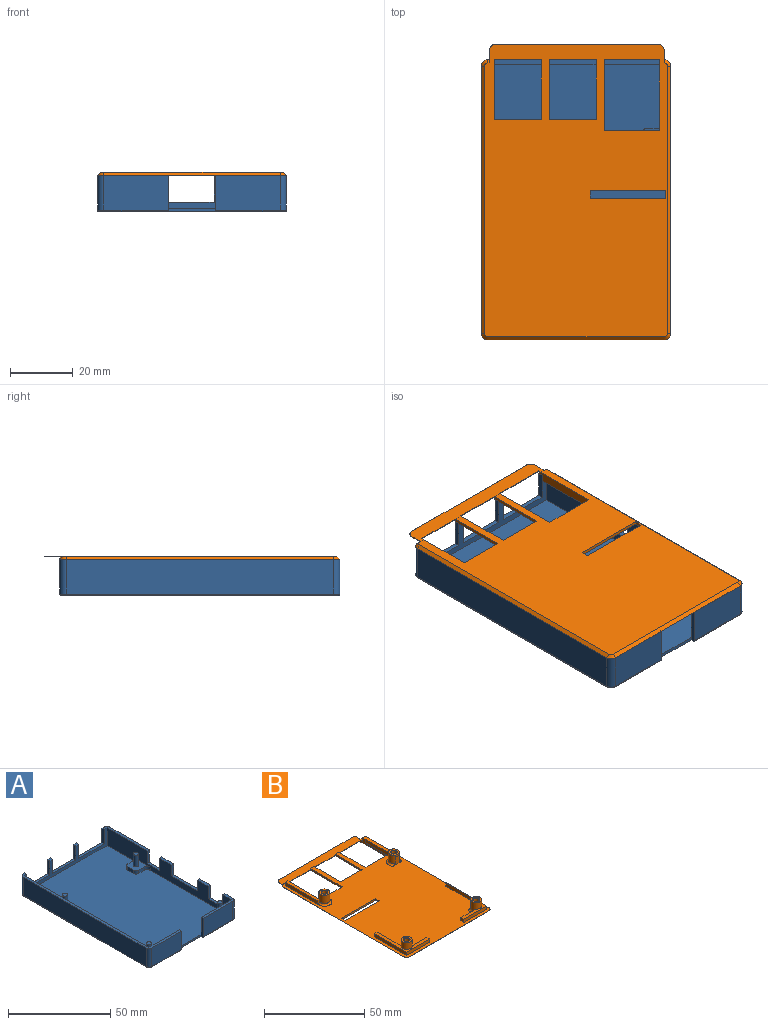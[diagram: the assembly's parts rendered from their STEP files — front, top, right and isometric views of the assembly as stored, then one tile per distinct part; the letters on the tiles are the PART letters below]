
ASSEMBLY  parts=2 mates=1
PART A: 89 faces, bbox 60.3x89.3x11.5 mm
  f0: plane 8.25x1.5mm, normal (0,0,1), area 12.4mm2, adj f3,f17,f84,f88
  f1: plane 29.25x3.5mm, normal (0,0,1), area 46mm2, adj f3,f16,f17,f18,f21,f70,f85
  f2: plane 7.5x1.5mm, normal (0,0,1), area 11.2mm2, adj f3,f17,f82,f87
  f3: plane 86x10.5mm, normal (-1,0,0), area 604.7mm2, adj f0,f1,f2,f4,f5,f8,f18,f35
  f4: plane 21x10.5mm, normal (0,1,0), area 201mm2, adj f3,f5,f8,f30,f39,f54
  f5: plane 86x57mm, normal (0,0,1), area 4663.9mm2, adj f3,f4,f6,f7,f18,f28,f32,f33
  f6: plane 86x10.5mm, normal (1,0,0), area 860.5mm2, adj f5,f7,f12,f18,f31,f42,f58,f59
  f7: plane 21x10.5mm, normal (0,1,0), area 201mm2, adj f5,f6,f12,f29,f42,f53
  f8: plane 22.5x7.5mm, normal (0,0,1), area 41.9mm2, adj f3,f4,f9,f17,f30,f69,f81
  f9: plane 20.5x11mm, normal (0,-1,0), area 225.5mm2, adj f8,f30,f69,f79
  f10: plane 2x1.5mm, normal (0,0,1), area 3mm2, adj f16,f18,f23,f27
  f11: plane 2x1.5mm, normal (0,0,1), area 3mm2, adj f16,f18,f20,f24
  f12: plane 89x22.5mm, normal (0,0,1), area 165.5mm2, adj f6,f7,f13,f15,f16,f18,f26,f29
  f13: plane 85x11mm, normal (-1,0,0), area 935mm2, adj f12,f67,f68,f73
  f14: plane 88x59mm, normal (0,0,-1), area 5175.1mm2, adj f28,f29,f30,f71,f72,f73,f74,f75
  f15: plane 20.5x11mm, normal (0,-1,0), area 225.5mm2, adj f12,f29,f68,f71
  f16: plane 56x11mm, normal (0,1,0), area 195.3mm2, adj f1,f10,f11,f12,f19,f20,f21,f22
  f17: plane 85x11mm, normal (1,0,0), area 679.2mm2, adj f0,f1,f2,f8,f69,f70,f77,f80
  f18: plane 57x10.5mm, normal (0,-1,0), area 177.8mm2, adj f1,f3,f5,f6,f10,f11,f12,f19
  f19: plane 17.5x1.5mm, normal (0,0,1), area 26.2mm2, adj f16,f18,f20,f21
  f20: plane 8.5x1.5mm, normal (1,0,0), area 12.8mm2, adj f11,f16,f18,f19
  f21: plane 8.5x1.5mm, normal (-1,0,0), area 12.8mm2, adj f1,f16,f18,f19
  f22: plane 16x1.5mm, normal (0,0,1), area 24mm2, adj f16,f18,f23,f24
  f23: plane 8.5x1.5mm, normal (1,0,0), area 12.8mm2, adj f10,f16,f18,f22
  f24: plane 8.5x1.5mm, normal (-1,0,0), area 12.8mm2, adj f11,f16,f18,f22
  f25: plane 16x1.5mm, normal (0,0,1), area 24mm2, adj f16,f18,f26,f27
  f26: plane 8.5x1.5mm, normal (1,0,0), area 12.8mm2, adj f12,f16,f18,f25
  f27: plane 8.5x1.5mm, normal (-1,0,0), area 12.8mm2, adj f10,f16,f18,f25
  f28: plane 15x1mm, normal (0,-1,0), area 15mm2, adj f5,f14,f29,f30
  f29: plane 11.5x1.5mm, normal (1,0,0), area 17.2mm2, adj f7,f12,f14,f15,f28,f71
  f30: plane 11.5x1.5mm, normal (-1,0,0), area 17.2mm2, adj f4,f8,f9,f14,f28,f79
  f31: plane 11.5x7.75mm, normal (0,0,1), area 53.2mm2, adj f6,f32,f33,f34,f46,f59,f60,f65
  f32: plane 3.75x2mm, normal (0,-1,0), area 7.5mm2, adj f5,f31,f59,f65
  f33: plane 3.75x2mm, normal (0,1,0), area 7.5mm2, adj f5,f31,f60,f66
  f34: plane 3.5x2mm, normal (1,0,0), area 7mm2, adj f5,f31,f65,f66
  f35: plane 11.5x7.75mm, normal (0,0,1), area 53.2mm2, adj f3,f36,f37,f38,f48,f55,f56,f63
  f36: plane 3.5x2mm, normal (-1,0,0), area 7mm2, adj f5,f35,f63,f64
  f37: plane 3.75x2mm, normal (0,-1,0), area 7.5mm2, adj f5,f35,f55,f64
  f38: plane 3.75x2mm, normal (0,1,0), area 7.5mm2, adj f5,f35,f56,f63
  f39: plane 9.75x9.75mm, normal (0,0,1), area 56mm2, adj f3,f4,f40,f41,f50,f54,f57,f61
  f40: plane 3.75x2mm, normal (-1,0,0), area 7.5mm2, adj f5,f39,f54,f61
  f41: plane 3.75x2mm, normal (0,1,0), area 7.5mm2, adj f5,f39,f57,f61
  f42: plane 9.75x9.75mm, normal (0,0,1), area 56mm2, adj f6,f7,f43,f44,f52,f53,f58,f62
  f43: plane 3.75x2mm, normal (0,1,0), area 7.5mm2, adj f5,f42,f58,f62
  f44: plane 3.75x2mm, normal (1,0,0), area 7.5mm2, adj f5,f42,f53,f62
  f45: plane 2.5x2.5mm, normal (0,0,1), area 4.9mm2, adj f46
  f46: cylinder r=1.25mm len=7mm, axis (0,0,-1), area 55mm2, adj f31,f45
  f47: plane 2.5x2.5mm, normal (0,0,1), area 4.9mm2, adj f48
  f48: cylinder r=1.25mm len=7mm, axis (0,0,-1), area 55mm2, adj f35,f47
  f49: plane 2.5x2.5mm, normal (0,0,1), area 4.9mm2, adj f50
  f50: cylinder r=1.25mm len=7mm, axis (0,0,-1), area 55mm2, adj f39,f49
  f51: plane 2.5x2.5mm, normal (0,0,1), area 4.9mm2, adj f52
  f52: cylinder r=1.25mm len=7mm, axis (0,0,-1), area 55mm2, adj f42,f51
  f53: cylinder r=2mm len=2mm, axis (0,0,-1), area 6.3mm2, adj f5,f7,f42,f44
  f54: cylinder r=2mm len=2mm, axis (0,0,1), area 6.3mm2, adj f4,f5,f39,f40
  f55: cylinder r=2mm len=2mm, axis (0,0,1), area 6.3mm2, adj f3,f5,f35,f37
  f56: cylinder r=2mm len=2mm, axis (0,0,-1), area 6.3mm2, adj f3,f5,f35,f38
  f57: cylinder r=2mm len=2mm, axis (0,0,-1), area 6.3mm2, adj f3,f5,f39,f41
  f58: cylinder r=2mm len=2mm, axis (0,0,-1), area 6.3mm2, adj f5,f6,f42,f43
  f59: cylinder r=2mm len=2mm, axis (0,0,1), area 6.3mm2, adj f5,f6,f31,f32
  f60: cylinder r=2mm len=2mm, axis (0,0,-1), area 6.3mm2, adj f5,f6,f31,f33
  f61: cylinder r=2mm len=2mm, axis (0,0,1), area 6.3mm2, adj f5,f39,f40,f41
  f62: cylinder r=2mm len=2mm, axis (0,0,-1), area 6.3mm2, adj f5,f42,f43,f44
  f63: cylinder r=2mm len=2mm, axis (0,0,1), area 6.3mm2, adj f5,f35,f36,f38
  f64: cylinder r=2mm len=2mm, axis (0,0,-1), area 6.3mm2, adj f5,f35,f36,f37
  f65: cylinder r=2mm len=2mm, axis (0,0,1), area 6.3mm2, adj f5,f31,f32,f34
  f66: cylinder r=2mm len=2mm, axis (0,0,-1), area 6.3mm2, adj f5,f31,f33,f34
  f67: cylinder r=2mm len=11mm, axis (0,0,1), area 34.6mm2, adj f12,f13,f16,f74
  f68: cylinder r=2mm len=11mm, axis (0,0,-1), area 34.6mm2, adj f12,f13,f15,f72
  f69: cylinder r=2mm len=11mm, axis (0,0,1), area 34.6mm2, adj f8,f9,f17,f78
  f70: cylinder r=2mm len=11mm, axis (0,0,-1), area 34.6mm2, adj f1,f16,f17,f76
  f71: cylinder r=0.5mm len=20.5mm, axis (1,0,0), area 16.1mm2, adj f14,f15,f29,f72
  f72: torus R=1.5mm, axis (0,0,1), area 2.2mm2, adj f14,f68,f71,f73
  f73: cylinder r=0.5mm len=85mm, axis (0,-1,0), area 66.8mm2, adj f13,f14,f72,f74
  f74: torus R=1.5mm, axis (0,0,1), area 2.2mm2, adj f14,f67,f73,f75
  f75: cylinder r=0.5mm len=56mm, axis (-1,0,0), area 44mm2, adj f14,f16,f74,f76
  f76: torus R=1.5mm, axis (0,0,1), area 2.2mm2, adj f14,f70,f75,f77
  f77: cylinder r=0.5mm len=85mm, axis (0,1,0), area 66.8mm2, adj f14,f17,f76,f78
  f78: torus R=1.5mm, axis (0,0,1), area 2.2mm2, adj f14,f69,f77,f79
  f79: cylinder r=0.5mm len=20.5mm, axis (1,0,0), area 16.1mm2, adj f9,f14,f30,f78
  f80: plane 10x1.5mm, normal (0,0,1), area 15mm2, adj f3,f17,f81,f82
  f81: plane 7.5x1.5mm, normal (0,1,0), area 11.2mm2, adj f3,f8,f17,f80
  f82: plane 7.5x1.5mm, normal (0,-1,0), area 11.2mm2, adj f2,f3,f17,f80
  f83: plane 8.5x1.5mm, normal (0,0,1), area 12.8mm2, adj f3,f17,f84,f85
  f84: plane 7.5x1.5mm, normal (0,1,0), area 11.2mm2, adj f0,f3,f17,f83
  f85: plane 7.5x1.5mm, normal (0,-1,0), area 11.2mm2, adj f1,f3,f17,f83
  f86: plane 18x1.5mm, normal (0,0,1), area 27mm2, adj f3,f17,f87,f88
  f87: plane 6.5x1.5mm, normal (0,1,0), area 9.7mm2, adj f2,f3,f17,f86
  f88: plane 6.5x1.5mm, normal (0,-1,0), area 9.7mm2, adj f0,f3,f17,f86
PART B: 90 faces, bbox 60.1x94.1x7.1 mm
  f0: cylinder r=2.75mm len=5.5mm, axis (0,0,-1), area 75.5mm2, adj f1,f2,f12,f13,f16,f38,f88,f89
  f1: torus R=3.75mm, axis (0,0,1), area 15.2mm2, adj f0,f6,f13,f89
  f2: torus R=3.75mm, axis (0,0,1), area 6.2mm2, adj f0,f6,f12,f89
  f3: torus R=3.75mm, axis (0,0,1), area 7.5mm2, adj f6,f11,f17,f40
  f4: plane 51.48x0.2mm, normal (0,1,0), area 10.3mm2, adj f5,f7,f64,f65
  f5: plane 55.48x5.8mm, normal (0,0,1), area 278.1mm2, adj f4,f15,f34,f44,f48,f52,f57,f58
  f6: plane 89x59.99mm, normal (0,0,1), area 3980.2mm2, adj f1,f2,f3,f8,f9,f11,f12,f13
  f7: plane 93x57.99mm, normal (0,0,-1), area 4351.7mm2, adj f4,f15,f34,f43,f44,f45,f46,f47
  f8: plane 10.38x2mm, normal (0,1,0), area 20.5mm2, adj f6,f24,f28,f41,f63
  f9: plane 16.88x2mm, normal (1,0,0), area 33.5mm2, adj f6,f24,f25,f41,f63
  f10: plane 1.82x0.48mm, normal (-1,0,0), area 0.6mm2, adj f17,f18,f40,f62
  f11: plane 10.37x2mm, normal (0,1,0), area 20.5mm2, adj f3,f6,f18,f21,f40
  f12: plane 2.09x1.29mm, normal (0,-1,0), area 2.2mm2, adj f0,f2,f6,f16,f32
  f13: plane 19.64x2mm, normal (-1,0,0), area 39mm2, adj f0,f1,f6,f16,f35
  f14: plane 2.09x1.28mm, normal (0,-1,0), area 2.2mm2, adj f6,f29,f31,f36,f61
  f15: plane 23.62x3mm, normal (1,0,0), area 65.6mm2, adj f5,f6,f7,f29,f30,f36,f43,f44
  f16: plane 22.75x2.25mm, normal (0,0,1), area 45.5mm2, adj f0,f12,f13,f32,f33,f34,f35
  f17: plane 6.3x5mm, normal (0,1,0), area 15.6mm2, adj f3,f6,f10,f18,f22,f40,f62,f87
  f18: plane 28.59x16.25mm, normal (0,0,1), area 40.8mm2, adj f10,f11,f17,f19,f20,f21,f22,f23
  f19: plane 28.59x2mm, normal (1,0,0), area 57.2mm2, adj f6,f18,f20,f23
  f20: plane 16.25x2mm, normal (0,-1,0), area 32.5mm2, adj f6,f18,f19,f21
  f21: plane 2x2mm, normal (-1,0,0), area 4mm2, adj f6,f11,f18,f20
  f22: plane 22.34x2mm, normal (-1,0,0), area 44.7mm2, adj f6,f17,f18,f23
  f23: plane 2x0.25mm, normal (0,1,0), area 0.5mm2, adj f6,f18,f19,f22
  f24: plane 22.75x16.25mm, normal (0,0,1), area 68.2mm2, adj f8,f9,f25,f26,f27,f28,f41
  f25: plane 2x2mm, normal (0,1,0), area 4mm2, adj f6,f9,f24,f26
  f26: plane 22.75x2mm, normal (-1,0,0), area 45.5mm2, adj f6,f24,f25,f27
  f27: plane 16.25x2mm, normal (0,-1,0), area 32.5mm2, adj f6,f24,f26,f28
  f28: plane 2x2mm, normal (1,0,0), area 4mm2, adj f6,f8,f24,f27
  f29: plane 22.75x1.75mm, normal (0,0,1), area 39.5mm2, adj f14,f15,f30,f31,f36
  f30: plane 2x1.75mm, normal (0,1,0), area 3.5mm2, adj f6,f15,f29,f31
  f31: plane 22.75x2mm, normal (-1,0,0), area 45.5mm2, adj f6,f14,f29,f30
  f32: plane 22.75x2mm, normal (1,0,0), area 45.5mm2, adj f6,f12,f16,f33
  f33: plane 2.25x2mm, normal (0,1,0), area 4.5mm2, adj f6,f16,f32,f34
  f34: plane 19x3mm, normal (-1,0,0), area 22.7mm2, adj f5,f6,f7,f16,f33,f35,f50,f52
  f35: plane 2x0.25mm, normal (0,-1,0), area 0.5mm2, adj f6,f13,f16,f34
  f36: cylinder r=2.75mm len=5.5mm, axis (0,0,-1), area 85.3mm2, adj f14,f15,f29,f37,f61
  f37: plane 5.5x5.5mm, normal (0,0,1), area 14.7mm2, adj f36,f86
  f38: plane 5.5x5.5mm, normal (0,0,1), area 14.7mm2, adj f0,f85
  f39: plane 5.5x5.5mm, normal (0,0,1), area 14.7mm2, adj f40,f84
  f40: cylinder r=2.75mm len=5.5mm, axis (0,0,-1), area 67.8mm2, adj f3,f10,f11,f17,f18,f39,f62,f87
  f41: cylinder r=2.75mm len=5.5mm, axis (0,0,-1), area 77.2mm2, adj f8,f9,f24,f42,f63
  f42: plane 5.5x5.5mm, normal (0,0,1), area 14.7mm2, adj f41,f83
  f43: plane 17.5x1.34mm, normal (0,1,0), area 18.2mm2, adj f6,f7,f15,f45,f61
  f44: plane 17.5x0.2mm, normal (0,-1,0), area 3.5mm2, adj f5,f7,f15,f45
  f45: plane 22.5x1mm, normal (-1,0,0), area 22.5mm2, adj f6,f7,f43,f44,f57
  f46: plane 15x1mm, normal (0,1,0), area 15mm2, adj f6,f7,f47,f49
  f47: plane 19x1mm, normal (1,0,0), area 19mm2, adj f6,f7,f46,f48,f57
  f48: plane 15x0.2mm, normal (0,-1,0), area 3mm2, adj f5,f7,f47,f49
  f49: plane 19x1mm, normal (-1,0,0), area 19mm2, adj f6,f7,f46,f48,f58
  f50: plane 15x1mm, normal (0,1,0), area 15mm2, adj f6,f7,f34,f51
  f51: plane 19x1mm, normal (1,0,0), area 19mm2, adj f6,f7,f50,f52,f58
  f52: plane 15x0.2mm, normal (0,-1,0), area 3mm2, adj f5,f7,f34,f51
  f53: plane 24x1mm, normal (0,1,0), area 24mm2, adj f6,f7,f54,f56
  f54: plane 2.5x1mm, normal (1,0,0), area 2.5mm2, adj f6,f7,f53,f55
  f55: plane 24x1mm, normal (0,-1,0), area 24mm2, adj f6,f7,f54,f56
  f56: plane 2.5x1mm, normal (-1,0,0), area 2.5mm2, adj f6,f7,f53,f55
  f57: plane 2.5x0.8mm, normal (0,1,0), area 2mm2, adj f5,f6,f45,f47
  f58: plane 2.5x0.8mm, normal (0,1,0), area 2mm2, adj f5,f6,f49,f51
  f59: plane 4x0.2mm, normal (-1,0,0), area 0.8mm2, adj f5,f7,f65,f66
  f60: plane 4x0.2mm, normal (1,0,0), area 0.8mm2, adj f5,f7,f64,f74
  f61: torus R=3.75mm, axis (0,0,1), area 25.6mm2, adj f6,f14,f15,f36,f43
  f62: torus R=3.75mm, axis (0,0,1), area 0.4mm2, adj f10,f17,f40
  f63: torus R=3.75mm, axis (0,0,1), area 13.5mm2, adj f6,f8,f9,f41
  f64: cylinder r=2mm len=2mm, axis (0,0,1), area 0.6mm2, adj f4,f5,f7,f60
  f65: cylinder r=2mm len=2mm, axis (0,0,-1), area 0.6mm2, adj f4,f5,f7,f59
  f66: plane 1.49x1mm, normal (0,0.71,-0.71), area 1.7mm2, adj f5,f6,f7,f15,f59,f67
  f67: cone r=1mm half-angle=45deg, axis (0,0,1), area 3.3mm2, adj f6,f7,f66,f68
  f68: plane 85x1mm, normal (-0.71,0,-0.71), area 120.2mm2, adj f6,f7,f67,f69
  f69: cone r=1mm half-angle=45deg, axis (0,0,1), area 3.3mm2, adj f6,f7,f68,f70
  f70: plane 55.99x1mm, normal (0,-0.71,-0.71), area 79.2mm2, adj f6,f7,f69,f71
  f71: cone r=1mm half-angle=45deg, axis (0,0,1), area 3.3mm2, adj f6,f7,f70,f72
  f72: plane 85x1mm, normal (0.71,0,-0.71), area 120.2mm2, adj f6,f7,f71,f73
  f73: cone r=1mm half-angle=45deg, axis (0,0,1), area 3.3mm2, adj f6,f7,f72,f74
  f74: plane 2x1mm, normal (0,0.71,-0.71), area 2.4mm2, adj f5,f6,f7,f34,f60,f73
  f75: plane 3x3mm, normal (0,0,1), area 7.1mm2, adj f76
  f76: cylinder r=1.5mm len=5.8mm, axis (0,0,1), area 54.7mm2, adj f75,f83
  f77: plane 3x3mm, normal (0,0,1), area 7.1mm2, adj f78
  f78: cylinder r=1.5mm len=5.8mm, axis (0,0,1), area 54.7mm2, adj f77,f84
  f79: plane 3x3mm, normal (0,0,1), area 7.1mm2, adj f80
  f80: cylinder r=1.5mm len=5.8mm, axis (0,0,1), area 54.7mm2, adj f79,f85
  f81: plane 3x3mm, normal (0,0,1), area 7.1mm2, adj f82
  f82: cylinder r=1.5mm len=5.8mm, axis (0,0,1), area 54.7mm2, adj f81,f86
  f83: cone r=1.5mm half-angle=45deg, axis (0,0,1), area 2.8mm2, adj f42,f76
  f84: cone r=1.5mm half-angle=45deg, axis (0,0,1), area 2.8mm2, adj f39,f78
  f85: cone r=1.5mm half-angle=45deg, axis (0,0,1), area 2.8mm2, adj f38,f80
  f86: cone r=1.5mm half-angle=45deg, axis (0,0,1), area 2.8mm2, adj f37,f82
  f87: plane 2.28x0.25mm, normal (0,0,-1), area 0.4mm2, adj f17,f40
  f88: plane 2.29x0.25mm, normal (0,0,-1), area 0.4mm2, adj f0,f89
  f89: plane 5.59x5mm, normal (0,-1,0), area 12.3mm2, adj f0,f1,f2,f6,f88
PLACE A t=(5.92,15.67,13.98)mm
PLACE B rot(axis=(0,1,0),180deg) t=(2.92,59.17,26.48)mm
MATE fastened B.f6 <-> A.f12  axis (0,0,-1) through (-31.58,101.17,25.48)mm
